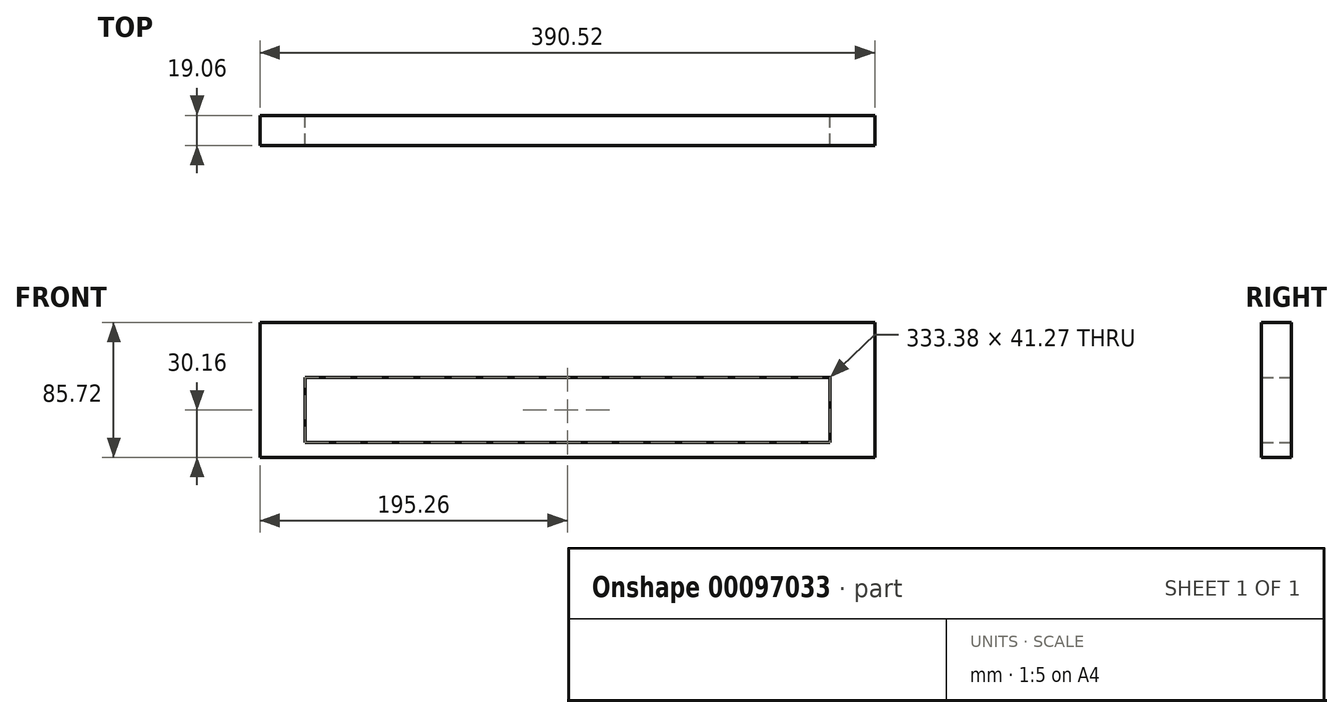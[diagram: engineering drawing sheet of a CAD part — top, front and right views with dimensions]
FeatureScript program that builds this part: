
annotation { "Feature Type Name" : "Feature", "Feature Type Description" : "" }
export const myFeature = defineFeature(function(context is Context, id is Id, definition is map)
    precondition{}
    {
        {
            var Q0;
            Q0=qCreatedBy(makeId("Front.planeOp"),FACE);
            var sketch = newSketch(context, id + "F0", { "sketchPlane" : qUnion([Q0])});
            skLineSegment(sketch, "E0.left", {"start": v(-166.69, 7.94) * mm, "end": v(-166.69, -33.34) * mm});
            skLineSegment(sketch, "E0.right", {"start": v(166.69, 7.94) * mm, "end": v(166.69, -33.34) * mm});
            skPoint(sketch, "E0.middle", {"position": v(0, 0) * mm});
            skLineSegment(sketch, "E1.bottom", {"start": v(-195.26, 42.86) * mm, "end": v(195.26, 42.86) * mm});
            skLineSegment(sketch, "E1.top", {"start": v(-195.26, -42.86) * mm, "end": v(195.26, -42.86) * mm});
            skLineSegment(sketch, "E1.left", {"start": v(-195.26, 42.86) * mm, "end": v(-195.26, -42.86) * mm});
            skLineSegment(sketch, "E1.right", {"start": v(195.26, 42.86) * mm, "end": v(195.26, -42.86) * mm});
            skLineSegment(sketch, "E2.0", {"start": v(-166.69, 7.94) * mm, "end": v(166.69, 7.94) * mm});
            skLineSegment(sketch, "E3.0", {"start": v(-166.69, -33.34) * mm, "end": v(166.69, -33.34) * mm});
            skSolve(sketch);
        }
        {
            var Q0;
            Q0=makeQuery(id+"F0.imprint","IMPRINT",FACE,{"disambiguationData":[TD([[makeQuery(id+"F0.imprint","IMPRINT",EDGE,{"derivedFrom":sQuery(id+"F0.wireOp",EDGE,"E0.left")}),-1.0]])]});
            extrude(context, id + "F1", {"entities" : qUnion([Q0]), "endBound" : BoundingType.SYMMETRIC, "depth" : 19.05 * mm});
        }
    });
